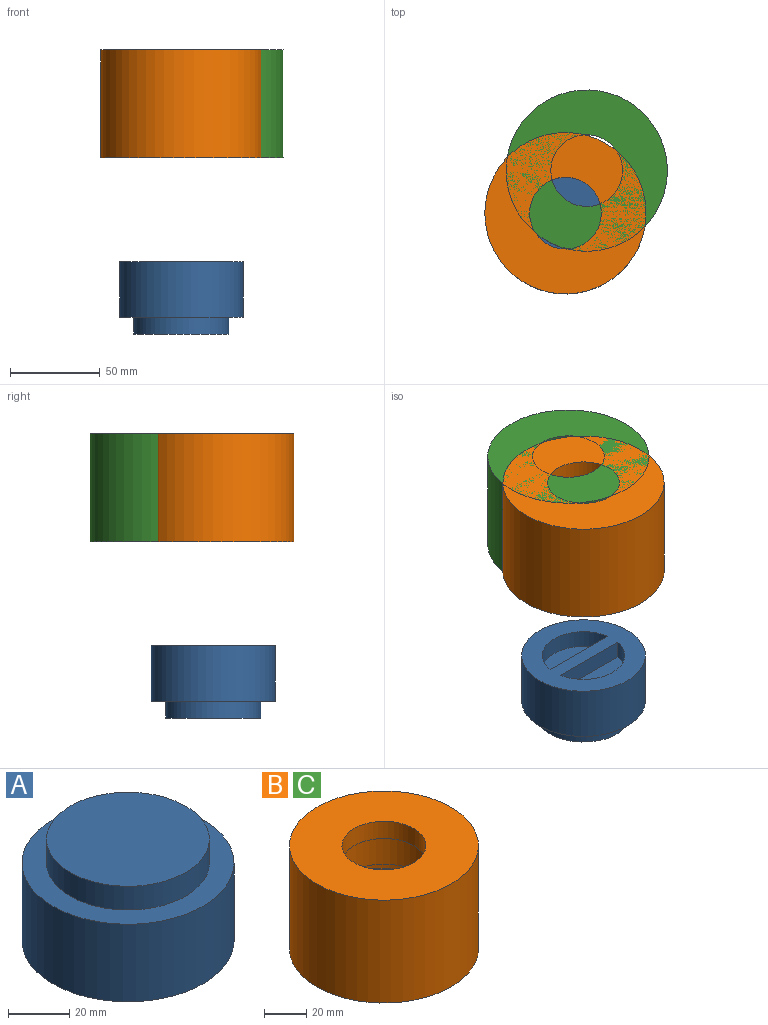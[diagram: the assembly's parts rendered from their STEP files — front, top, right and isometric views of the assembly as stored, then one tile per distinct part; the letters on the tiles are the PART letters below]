
ASSEMBLY  parts=3 mates=1
PART A: 11 faces, bbox 69x69x40.3 mm
  f0: plane 69x69mm, normal (0,0,-1), area 2448.3mm2, adj f3,f5,f6,f8,f9
  f1: cylinder r=26.5mm len=53mm, axis (0,0,-1), area 1571.3mm2, adj f2,f4
  f2: plane 69x69mm, normal (0,0,1), area 1533.1mm2, adj f1,f3
  f3: cylinder r=34.5mm len=69mm, axis (0,0,-1), area 6700.5mm2, adj f0,f2
  f4: plane 53x53mm, normal (0,0,1), area 2206.2mm2, adj f1
  f5: plane 45.44x10mm, normal (0,-1,0), area 454.4mm2, adj f0,f6,f7
  f6: cylinder r=23mm len=45.44mm, axis (0,0,-1), area 650.7mm2, adj f0,f5,f7
  f7: plane 45.44x19.42mm, normal (0,0,-1), area 666.9mm2, adj f5,f6
  f8: plane 45.1x10mm, normal (0,1,0), area 451mm2, adj f0,f9,f10
  f9: cylinder r=23mm len=45.1mm, axis (0,0,-1), area 631.4mm2, adj f0,f8,f10
  f10: plane 45.1x18.47mm, normal (0,0,-1), area 624mm2, adj f8,f9
PART B: 18 faces, bbox 91.8x91.8x64.9 mm
  f0: cylinder r=35mm len=70mm, axis (0,0,-1), area 1346.8mm2, adj f1,f5,f15,f16
  f1: cylinder r=35mm len=70mm, axis (0,0,-1), area 164.6mm2, adj f0,f2,f16
  f2: cylinder r=35mm len=70mm, axis (0,0,-1), area 164.6mm2, adj f1,f3,f16
  f3: cylinder r=35mm len=70mm, axis (0,0,-1), area 154.5mm2, adj f2,f4,f16,f17
  f4: plane 91.8x91.8mm, normal (0,0,-1), area 2284.2mm2, adj f3,f14,f16,f17
  f5: plane 70x70mm, normal (0,0,-1), area 1558.2mm2, adj f0,f6
  f6: cylinder r=27mm len=54mm, axis (0,0,-1), area 3392.9mm2, adj f5,f7
  f7: plane 54x54mm, normal (0,0,-1), area 465.6mm2, adj f6,f8
  f8: cylinder r=24.1mm len=48.2mm, axis (0,0,-1), area 302.8mm2, adj f7,f9
  f9: plane 48.2x48.2mm, normal (0,0,-1), area 372.5mm2, adj f8,f10
  f10: cylinder r=21.5mm len=43mm, axis (0,0,-1), area 270.2mm2, adj f9,f11
  f11: plane 43x43mm, normal (0,0,-1), area 195.6mm2, adj f10,f12
  f12: cylinder r=20mm len=40mm, axis (0,0,-1), area 1256.6mm2, adj f11,f13
  f13: plane 90x90mm, normal (0,0,1), area 5105.1mm2, adj f12,f14
  f14: cylinder r=45mm len=90mm, axis (0,0,-1), area 16964.6mm2, adj f4,f13
  f15: plane 5.76x1.89mm, normal (0,-1,0), area 6.4mm2, adj f0,f16
  f16: bspline ~86.53x74.93mm, area 5885.8mm2, adj f0,f1,f2,f3,f4,f15,f17
  f17: bspline ~73.22x42.27mm, area 128mm2, adj f3,f4,f16
PART C: same geometry as B
PLACE A rot(axis=(1,0,0),180deg) t=(-35.96,-32.32,-83.97)mm
PLACE B t=(-35.96,-32.32,45.23)mm
PLACE C t=(-24.13,-8.57,45.23)mm
MATE slider A.f1 <-> B.f0  axis (0,0,1) through (-35.96,-32.32,-21.61)mm
